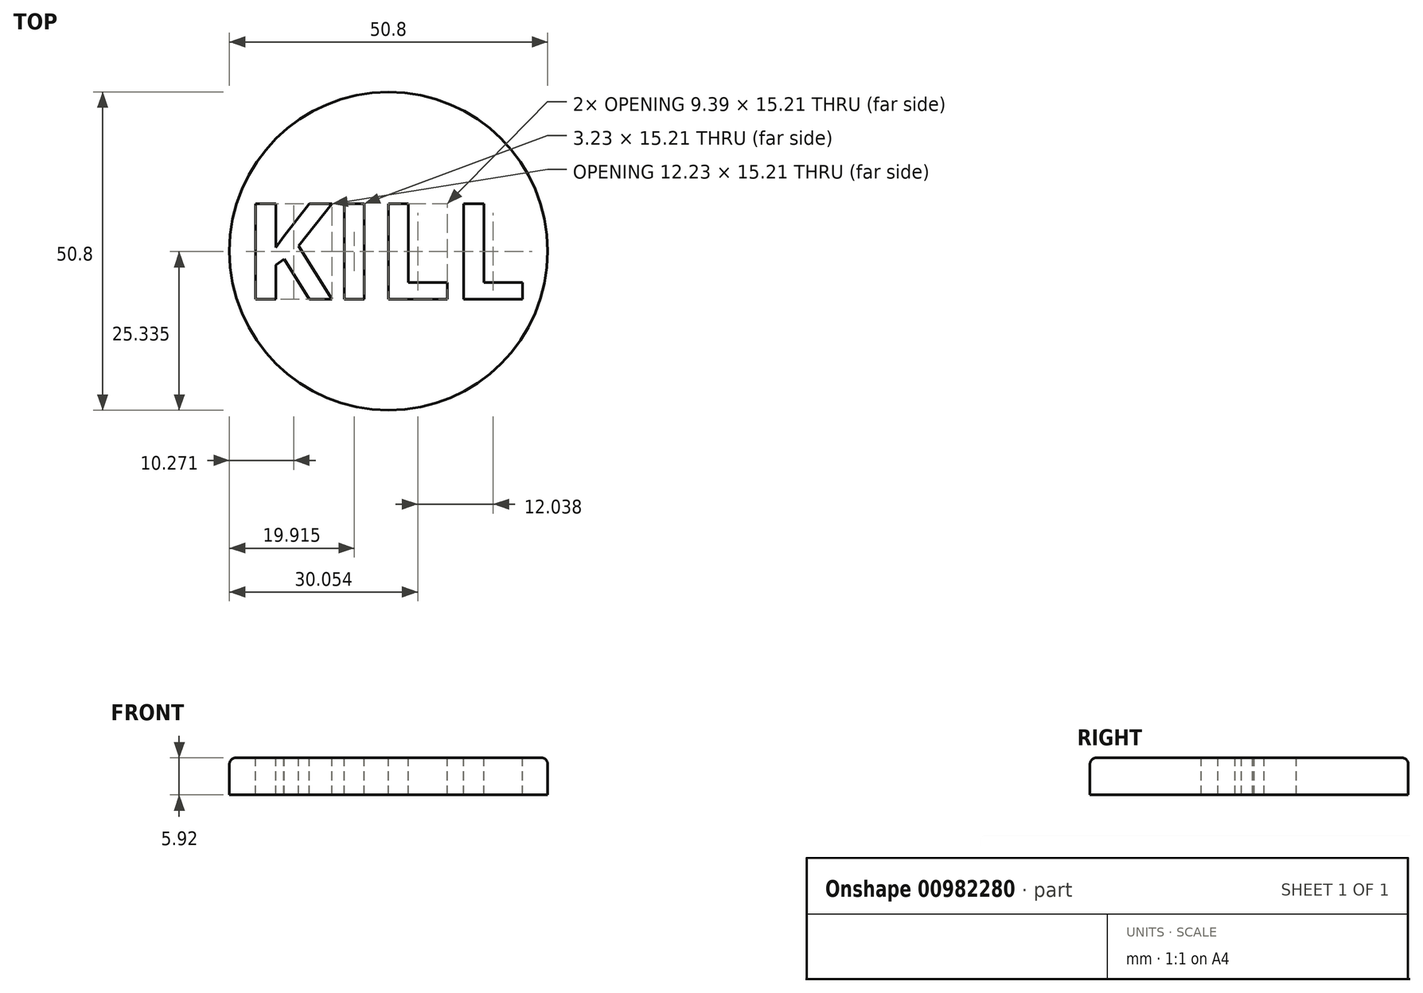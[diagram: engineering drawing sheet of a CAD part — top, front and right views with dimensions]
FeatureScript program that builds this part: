
annotation { "Feature Type Name" : "Feature", "Feature Type Description" : "" }
export const myFeature = defineFeature(function(context is Context, id is Id, definition is map)
    precondition{}
    {
        {
            var Q0;
            Q0=qCreatedBy(makeId("Top.planeOp"),FACE);
            var sketch = newSketch(context, id + "F0", { "sketchPlane" : qUnion([Q0])});
            skCircle(sketch, "E0", {"center": v(0, 0) * mm, "radius": 25.4 * mm});
            skSolve(sketch);
        }
        {
            var Q0;
            Q0 = qSketchRegion(id + "F0", true);
            extrude(context, id + "F1", {"entities" : qUnion([Q0]), "depth" : 5.92 * mm, "offsetDistance" : 25 * mm});
        }
        {
            var Q0;
            Q0=makeQuery(id+"F1.opExtrude","CAP_EDGE",EDGE,{"disambiguationData":[OSD([sQuery(id+"F0.wireOp",EDGE,"E0")])],"isStart":false});
            fillet(context, id + "F2", {"entities" : qUnion([Q0]), "radius" : 1 * mm, "tangentPropagation" : true, "allowEdgeOverflow" : false});
        }
        {
            var Q0;
            Q0=makeQuery(id+"F1.opExtrude","CAP_FACE",FACE,{"disambiguationData":[OSD([sQuery(id+"F0.wireOp",EDGE,"E0")])],"isStart":false});
            var sketch = newSketch(context, id + "F3", { "sketchPlane" : qUnion([Q0])});
            skText(sketch, "E1", { "text": "KILL", "fontName": "OpenSans-Bold.ttf"});
            const initialGuessF3  = {"E1": [-0.02316, -0.00767, 1, 0, 0.01534]};
            skSetInitialGuess(sketch, initialGuessF3);
            skSolve(sketch);
        }
        {
            var Q0;
            Q0 = qSketchRegion(id + "F3", true);
            extrude(context, id + "F4", {"entities" : qUnion([Q0]), "operationType" : NewBodyOperationType.REMOVE, "oppositeDirection" : true, "depth" : 25 * mm, "offsetDistance" : 25 * mm});
        }
    });
